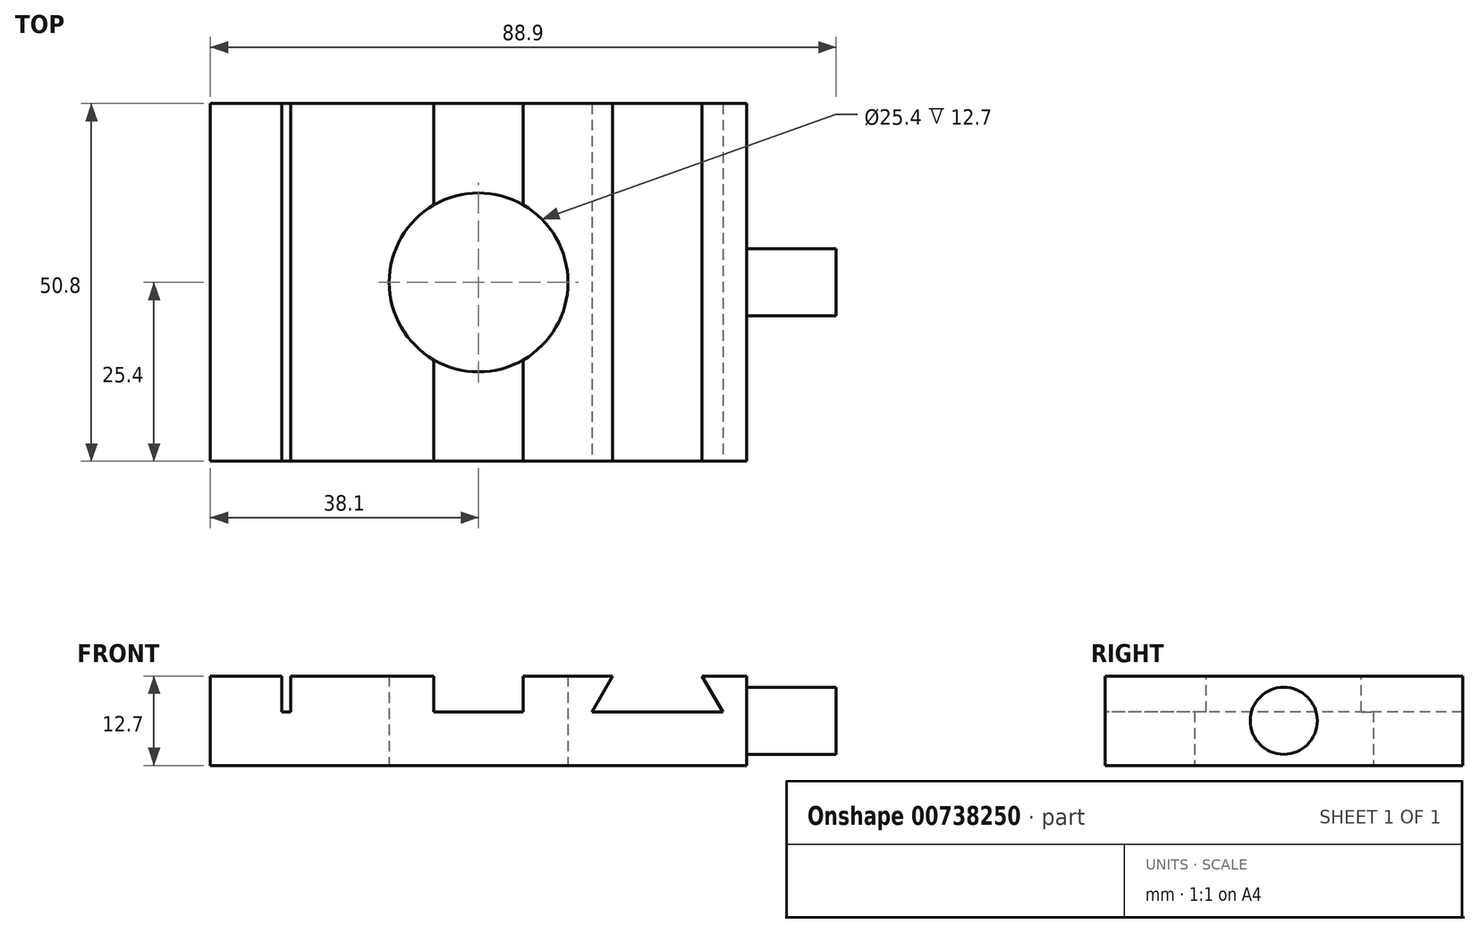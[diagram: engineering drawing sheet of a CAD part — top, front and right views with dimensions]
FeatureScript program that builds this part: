
annotation { "Feature Type Name" : "Feature", "Feature Type Description" : "" }
export const myFeature = defineFeature(function(context is Context, id is Id, definition is map)
    precondition{}
    {
        {
            var Q0;
            Q0=qCreatedBy(makeId("Top.planeOp"),FACE);
            var sketch = newSketch(context, id + "F0", { "sketchPlane" : qUnion([Q0])});
            skLineSegment(sketch, "E0.bottom", {"start": v(-38.1, 25.4) * mm, "end": v(38.1, 25.4) * mm});
            skLineSegment(sketch, "E0.top", {"start": v(-38.1, -25.4) * mm, "end": v(38.1, -25.4) * mm});
            skLineSegment(sketch, "E0.left", {"start": v(-38.1, 25.4) * mm, "end": v(-38.1, -25.4) * mm});
            skLineSegment(sketch, "E0.right", {"start": v(38.1, 25.4) * mm, "end": v(38.1, -25.4) * mm});
            skPoint(sketch, "E0.middle", {"position": v(0, 0) * mm});
            skCircle(sketch, "E1", {"center": v(0, 0) * mm, "radius": 12.7 * mm});
            skSolve(sketch);
        }
        {
            var Q0;
            Q0=makeQuery(id+"F0.imprint","IMPRINT",FACE,{"disambiguationData":[TD([[makeQuery(id+"F0.imprint","IMPRINT",EDGE,{"derivedFrom":sQuery(id+"F0.wireOp",EDGE,"E0.bottom")}),-1.0]])]});
            extrude(context, id + "F1", {"entities" : qUnion([Q0]), "depth" : 12.7 * mm, "offsetDistance" : 25.4 * mm});
        }
        {
            var Q0;
            Q0=makeQuery(id+"F1.opExtrude","CAP_FACE",FACE,{"disambiguationData":[OSD([sQuery(id+"F0.wireOp",EDGE,"E0.bottom"),sQuery(id+"F0.wireOp",EDGE,"E0.top"),sQuery(id+"F0.wireOp",EDGE,"E0.left"),sQuery(id+"F0.wireOp",EDGE,"E0.right"),sQuery(id+"F0.wireOp",EDGE,"E1")])],"isStart":false});
            var sketch = newSketch(context, id + "F2", { "sketchPlane" : qUnion([Q0])});
            skLineSegment(sketch, "E2.bottom", {"start": v(-27.94, 25.4) * mm, "end": v(-26.67, 25.4) * mm});
            skLineSegment(sketch, "E2.top", {"start": v(-27.94, -25.4) * mm, "end": v(-26.67, -25.4) * mm});
            skLineSegment(sketch, "E2.left", {"start": v(-27.94, 25.4) * mm, "end": v(-27.94, -25.4) * mm});
            skLineSegment(sketch, "E2.right", {"start": v(-26.67, 25.4) * mm, "end": v(-26.67, -25.4) * mm});
            skLineSegment(sketch, "E3", {"start": v(-6.35, 25.4) * mm, "end": v(-6.35, -25.4) * mm});
            skLineSegment(sketch, "E4", {"start": v(-6.35, -25.4) * mm, "end": v(6.35, -25.4) * mm});
            skLineSegment(sketch, "E5", {"start": v(6.35, -25.4) * mm, "end": v(6.35, 25.4) * mm});
            skLineSegment(sketch, "E6", {"start": v(6.35, 25.4) * mm, "end": v(-6.35, 25.4) * mm});
            skPoint(sketch, "E7", {"position": v(0, 0) * mm});
            skLineSegment(sketch, "E8", {"start": v(0, 25.4) * mm, "end": v(0, -25.4) * mm, "construction": true});
            skSolve(sketch);
        }
        {
            var Q0;
            Q0=makeQuery(id+"F2.imprint","IMPRINT",FACE,{"disambiguationData":[TD([[makeQuery(id+"F2.imprint","IMPRINT",EDGE,{"derivedFrom":sQuery(id+"F2.wireOp",EDGE,"E2.bottom")}),-1.0]])]});
            var Q1;
            {var subQ0=sQuery(id+"F2.wireOp",EDGE,"E6");Q1=makeQuery(id+"F2.imprint","IMPRINT",FACE,{"disambiguationData":[TD([[makeQuery(id+"F2.imprint","IMPRINT",EDGE,{"derivedFrom":subQ0}),-1.0]])]});}
            var Q2;
            {var subQ0=sQuery(id+"F2.wireOp",EDGE,"E4");Q2=makeQuery(id+"F2.imprint","IMPRINT",FACE,{"disambiguationData":[TD([[makeQuery(id+"F2.imprint","IMPRINT",EDGE,{"derivedFrom":subQ0}),1.0]])]});}
            extrude(context, id + "F3", {"entities" : qUnion([Q0, Q1, Q2]), "operationType" : NewBodyOperationType.REMOVE, "oppositeDirection" : true, "depth" : 5.08 * mm, "offsetDistance" : 25.4 * mm});
        }
        {
            var Q0;
            Q0=makeQuery(id+"F1.opExtrude","SWEPT_FACE",FACE,{"disambiguationData":[OSD([sQuery(id+"F0.wireOp",EDGE,"E0.top")])]});
            var sketch = newSketch(context, id + "F4", { "sketchPlane" : qUnion([Q0])});
            skLineSegment(sketch, "E9", {"start": v(19.05, 12.7) * mm, "end": v(16.12, 7.62) * mm});
            skLineSegment(sketch, "E10", {"start": v(16.12, 7.62) * mm, "end": v(34.68, 7.62) * mm});
            skLineSegment(sketch, "E11", {"start": v(34.68, 7.62) * mm, "end": v(31.75, 12.7) * mm});
            skLineSegment(sketch, "E12", {"start": v(25.4, 7.62) * mm, "end": v(25.4, 12.7) * mm, "construction": true});
            skPoint(sketch, "E12.endSnap0", {"position": v(25.4, 7.62) * mm});
            skSolve(sketch);
        }
        {
            var Q0;
            {var subQ0=sQuery(id+"F4.wireOp",EDGE,"E9");Q0=makeQuery(id+"F4.imprint","IMPRINT",FACE,{"disambiguationData":[TD([[makeQuery(id+"F4.imprint","IMPRINT",EDGE,{"derivedFrom":subQ0}),1.0]])]});}
            extrude(context, id + "F5", {"entities" : qUnion([Q0]), "operationType" : NewBodyOperationType.REMOVE, "endBound" : BoundingType.THROUGH_ALL, "oppositeDirection" : true, "depth" : 25.4 * mm, "offsetDistance" : 25.4 * mm});
        }
        {
            var Q0;
            Q0=makeQuery(id+"F1.opExtrude","SWEPT_FACE",FACE,{"disambiguationData":[OSD([sQuery(id+"F0.wireOp",EDGE,"E0.right")])]});
            var sketch = newSketch(context, id + "F6", { "sketchPlane" : qUnion([Q0])});
            skCircle(sketch, "E13", {"center": v(0, 6.35) * mm, "radius": 4.76 * mm});
            skPoint(sketch, "E13.centerSnap0", {"position": v(-25.4, 6.35) * mm});
            skPoint(sketch, "E13.centerSnap1", {"position": v(0, 12.7) * mm});
            skSolve(sketch);
        }
        {
            var Q0;
            Q0=makeQuery(id+"F6.imprint","IMPRINT",FACE,{"disambiguationData":[TD([[makeQuery(id+"F6.imprint","IMPRINT",EDGE,{"derivedFrom":sQuery(id+"F6.wireOp",EDGE,"E13")}),1.0]])]});
            extrude(context, id + "F7", {"entities" : qUnion([Q0]), "operationType" : NewBodyOperationType.ADD, "depth" : 12.7 * mm, "offsetDistance" : 25.4 * mm});
        }
    });
